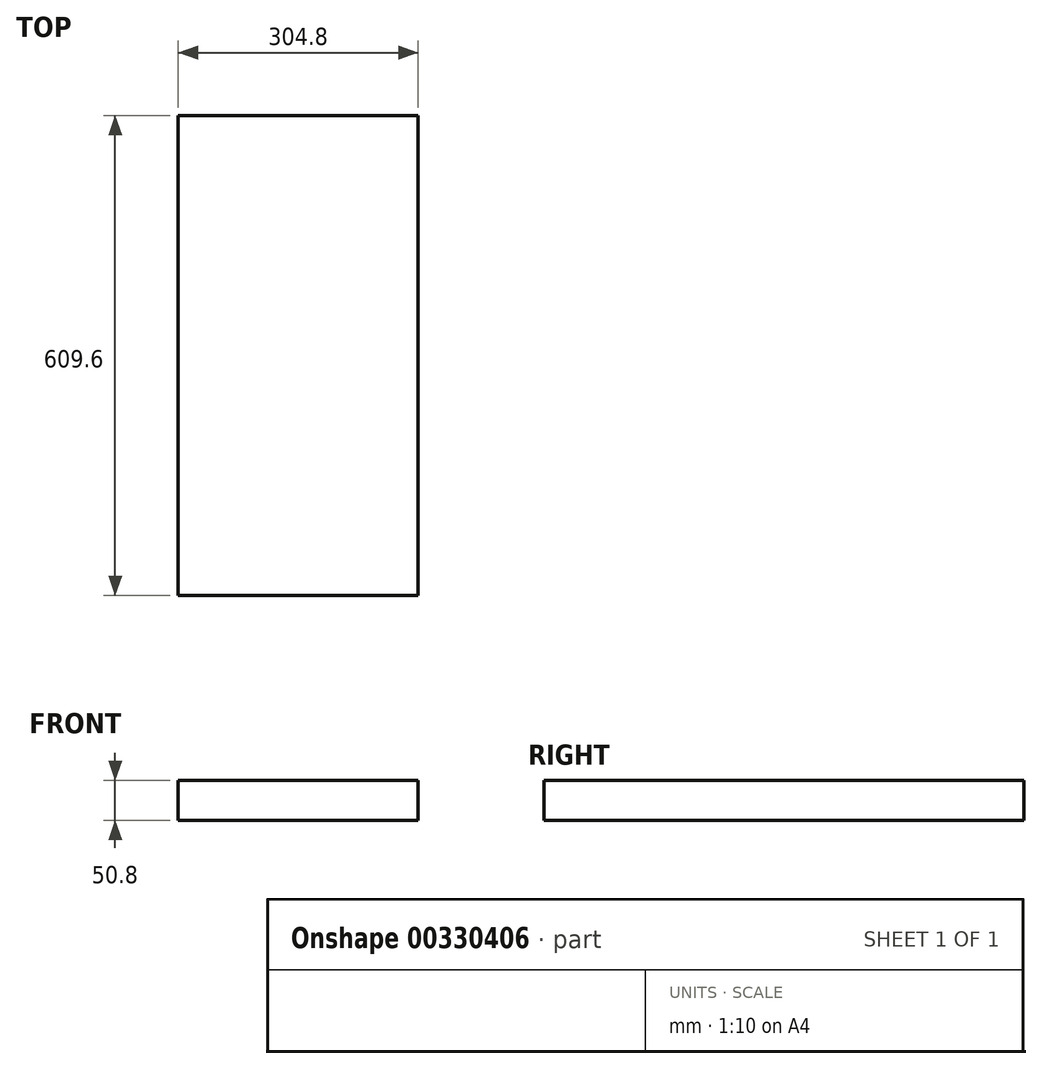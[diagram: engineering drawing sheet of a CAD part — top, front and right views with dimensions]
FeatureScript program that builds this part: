
annotation { "Feature Type Name" : "Feature", "Feature Type Description" : "" }
export const myFeature = defineFeature(function(context is Context, id is Id, definition is map)
    precondition{}
    {
        {
            var Q0;
            Q0=qCreatedBy(makeId("Top.planeOp"),FACE);
            var sketch = newSketch(context, id + "F0", { "sketchPlane" : qUnion([Q0])});
            skLineSegment(sketch, "E0.bottom", {"start": v(0, 0) * mm, "end": v(304.8, 0) * mm});
            skLineSegment(sketch, "E0.top", {"start": v(0, 609.6) * mm, "end": v(304.8, 609.6) * mm});
            skLineSegment(sketch, "E0.left", {"start": v(0, 0) * mm, "end": v(0, 609.6) * mm});
            skLineSegment(sketch, "E0.right", {"start": v(304.8, 0) * mm, "end": v(304.8, 609.6) * mm});
            skSolve(sketch);
        }
        {
            var Q0;
            Q0=makeQuery(id+"F0.imprint","IMPRINT",FACE,{"disambiguationData":[TD([[makeQuery(id+"F0.imprint","IMPRINT",EDGE,{"derivedFrom":sQuery(id+"F0.wireOp",EDGE,"E0.bottom")}),1.0]])]});
            extrude(context, id + "F1", {"entities" : qUnion([Q0]), "depth" : 50.8 * mm});
        }
    });
